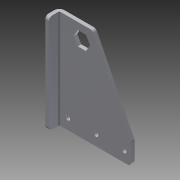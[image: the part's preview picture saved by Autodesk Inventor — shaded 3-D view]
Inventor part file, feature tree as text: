
AUTODESK INVENTOR PART (.ipt)
format: ipt  version: 2014 (Build 180170000, 170)  size: 189,952 bytes
history: native  units: in
note: dims shown in document units (in); Inventor stores cm internally (conversion verified against a paired STEP export)
features: sheet_metal_op x4, other x3, sketch x2, fillet x1, extrude x1
ambient origin geometry x8: Origin, YZ Plane, XZ Plane, XY Plane, X Axis, Y Axis, Z Axis, Center Point
bodies: Solid1 (feature_tree)
feature tree (11):
  sheet_metal_op  "Face1"
  sheet_metal_op  "Flange2"
  fillet  "Fillet1"  Radius=0.125in
  sketch  "Sketch1"  dims[d5=2.5in d6=0.163in d7=0.25in d8=0.375in d11=0.125in]
  other  "Plate1"
  sketch  "Sketch3"  dims[d22=1.1811in d24=1.0in d25=0.3937in d27=1.0in d29=3.5in d30=0.75in d31=1.125in d32=0.5in d34=0.75in d35=0.5in d36=0.125in d37=0.0625in d38=0.25in d39=0.125in d40=0.5in d41=90.0deg d42=0.05in d43=0.5in d44=0.125in d45=0.125in d46=0.125in d0=0.125in d2=0.0625in d4=1.0in]
  other  "Plate3"
  sheet_metal_op  "Bend2"
  sheet_metal_op  "Corner2"
  other  "Definition1"
  extrude  "Extrusion1"  Depth=3.5in
